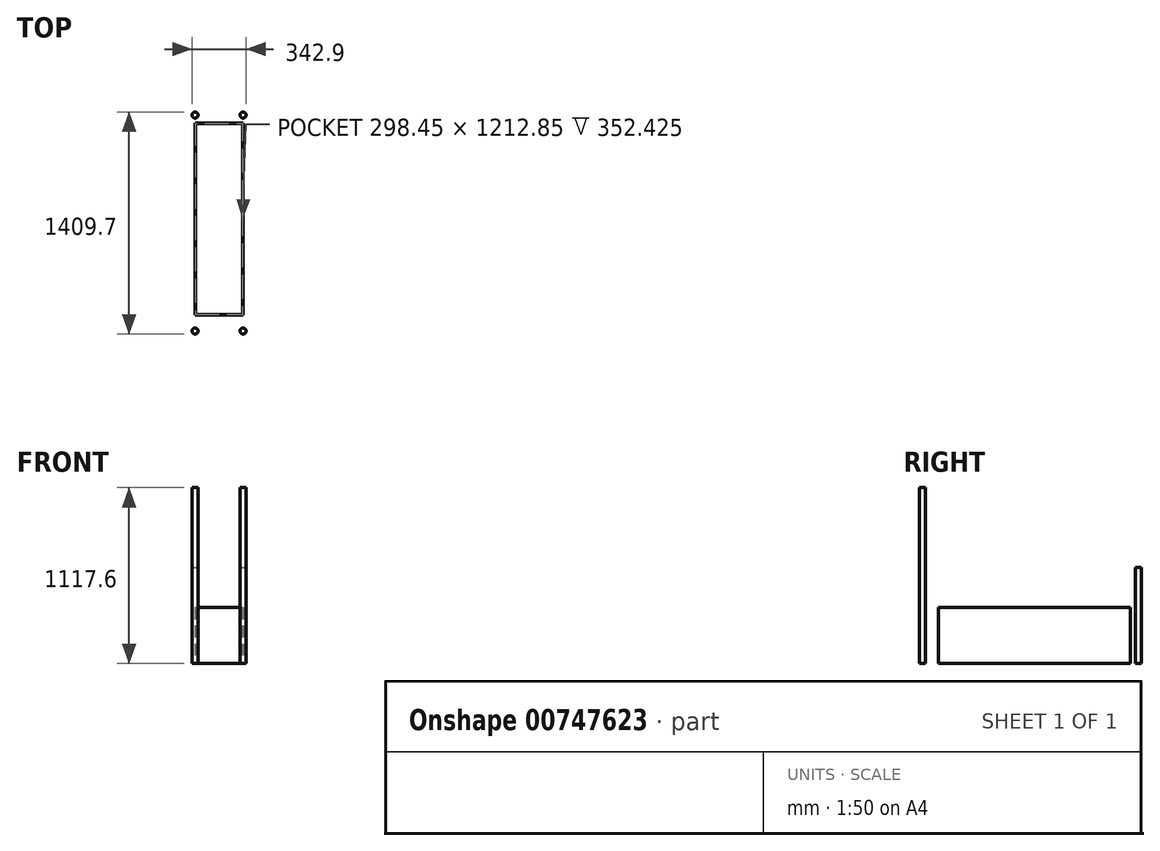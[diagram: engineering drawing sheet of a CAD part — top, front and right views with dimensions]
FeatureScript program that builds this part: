
annotation { "Feature Type Name" : "Feature", "Feature Type Description" : "" }
export const myFeature = defineFeature(function(context is Context, id is Id, definition is map)
    precondition{}
    {
        {
            var Q0;
            Q0=qCreatedBy(makeId("Top.planeOp"),FACE);
            var sketch = newSketch(context, id + "F0", { "sketchPlane" : qUnion([Q0])});
            skLineSegment(sketch, "E0.bottom", {"start": v(0, 0) * mm, "end": v(304.8, 0) * mm});
            skLineSegment(sketch, "E0.top", {"start": v(0, 1219.2) * mm, "end": v(304.8, 1219.2) * mm});
            skLineSegment(sketch, "E0.left", {"start": v(0, 0) * mm, "end": v(0, 1219.2) * mm});
            skLineSegment(sketch, "E0.right", {"start": v(304.8, 0) * mm, "end": v(304.8, 1219.2) * mm});
            skSolve(sketch);
        }
        {
            var Q0;
            Q0 = qSketchRegion(id + "F0", true);
            extrude(context, id + "F1", {"entities" : qUnion([Q0]), "depth" : 355.6 * mm, "offsetDistance" : 25.4 * mm});
        }
        {
            var Q0;
            Q0=makeQuery(id+"F1.opExtrude","CAP_FACE",FACE,{"disambiguationData":[OSD([sQuery(id+"F0.wireOp",EDGE,"E0.bottom"),sQuery(id+"F0.wireOp",EDGE,"E0.top"),sQuery(id+"F0.wireOp",EDGE,"E0.left"),sQuery(id+"F0.wireOp",EDGE,"E0.right")])],"isStart":false});
            shell(context, id + "F2", {"entities" : qUnion([Q0]), "thickness" : 3.17 * mm});
        }
        {
            var Q0;
            Q0=makeQuery(id+"F1.opExtrude","CAP_FACE",FACE,{"disambiguationData":[OSD([sQuery(id+"F0.wireOp",EDGE,"E0.bottom"),sQuery(id+"F0.wireOp",EDGE,"E0.top"),sQuery(id+"F0.wireOp",EDGE,"E0.left"),sQuery(id+"F0.wireOp",EDGE,"E0.right")])],"isStart":true});
            var sketch = newSketch(context, id + "F3", { "sketchPlane" : qUnion([Q0])});
            skLineSegment(sketch, "E1", {"start": v(0, 0) * mm, "end": v(0, 101.6) * mm, "construction": true});
            skLineSegment(sketch, "E2", {"start": v(304.8, 0) * mm, "end": v(304.8, 101.6) * mm, "construction": true});
            skCircle(sketch, "E3", {"center": v(0, 101.6) * mm, "radius": 19.05 * mm});
            skCircle(sketch, "E4", {"center": v(304.8, 101.6) * mm, "radius": 19.05 * mm});
            skSolve(sketch);
        }
        {
            var Q0;
            Q0 = qSketchRegion(id + "F3", true);
            extrude(context, id + "F4", {"entities" : qUnion([Q0]), "oppositeDirection" : true, "depth" : 1117.6 * mm, "offsetDistance" : 25.4 * mm});
        }
        {
            var Q0;
            Q0=makeQuery(id+"F1.opExtrude","CAP_FACE",FACE,{"disambiguationData":[OSD([sQuery(id+"F0.wireOp",EDGE,"E0.bottom"),sQuery(id+"F0.wireOp",EDGE,"E0.top"),sQuery(id+"F0.wireOp",EDGE,"E0.left"),sQuery(id+"F0.wireOp",EDGE,"E0.right")])],"isStart":true});
            var sketch = newSketch(context, id + "F5", { "sketchPlane" : qUnion([Q0])});
            skLineSegment(sketch, "E5", {"start": v(304.8, -1219.2) * mm, "end": v(304.8, -1270) * mm, "construction": true});
            skLineSegment(sketch, "E6", {"start": v(0, -1219.2) * mm, "end": v(0, -1270) * mm, "construction": true});
            skCircle(sketch, "E7", {"center": v(0, -1270) * mm, "radius": 19.05 * mm});
            skCircle(sketch, "E8", {"center": v(304.8, -1270) * mm, "radius": 19.05 * mm});
            skSolve(sketch);
        }
        {
            var Q0;
            Q0=makeQuery(id+"F5.imprint","IMPRINT",FACE,{"disambiguationData":[TD([[makeQuery(id+"F5.imprint","IMPRINT",EDGE,{"derivedFrom":sQuery(id+"F5.wireOp",EDGE,"E7")}),1.0]])]});
            var Q1;
            Q1=makeQuery(id+"F5.imprint","IMPRINT",FACE,{"disambiguationData":[TD([[makeQuery(id+"F5.imprint","IMPRINT",EDGE,{"derivedFrom":sQuery(id+"F5.wireOp",EDGE,"E8")}),1.0]])]});
            extrude(context, id + "F6", {"entities" : qUnion([Q0, Q1]), "oppositeDirection" : true, "depth" : 609.6 * mm, "offsetDistance" : 25.4 * mm});
        }
    });
